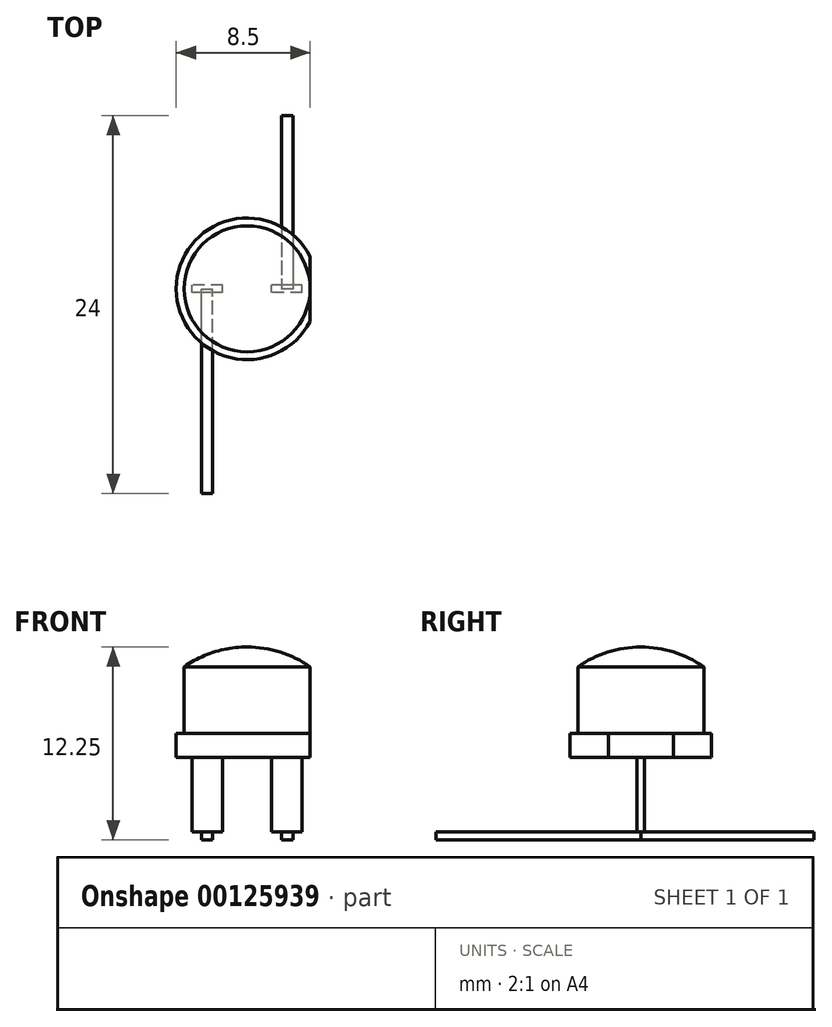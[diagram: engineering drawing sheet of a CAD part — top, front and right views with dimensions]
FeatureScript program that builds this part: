
annotation { "Feature Type Name" : "Feature", "Feature Type Description" : "" }
export const myFeature = defineFeature(function(context is Context, id is Id, definition is map)
    precondition{}
    {
        {
            var Q0;
            Q0=qCreatedBy(makeId("Front.planeOp"),FACE);
            var sketch = newSketch(context, id + "F0", { "sketchPlane" : qUnion([Q0])});
            skLineSegment(sketch, "E0", {"start": v(0, 0) * mm, "end": v(-4.5, 0) * mm});
            skLineSegment(sketch, "E1", {"start": v(-4.5, 0) * mm, "end": v(-4.5, 1.5) * mm});
            skLineSegment(sketch, "E2", {"start": v(-4.5, 1.5) * mm, "end": v(-4, 1.5) * mm});
            skLineSegment(sketch, "E3", {"start": v(-4, 1.5) * mm, "end": v(-4, 5.74) * mm});
            skLineSegment(sketch, "E4", {"start": v(0, 0) * mm, "end": v(0, 7) * mm});
            skArc(sketch, "E5", {"start": v(0, 7) * mm, "mid": v(-2.1, 6.68) * mm, "end": v(-4, 5.74) * mm});
            skSolve(sketch);
        }
        {
            var Q0;
            Q0=qSketchRegion(id+"F0",true);
            var Q1;
            Q1=sQuery(id+"F0.wireOp",EDGE,"E4");
            revolve(context, id + "F1", {"entities" : qUnion([Q0]), "axis" : qUnion([Q1]), "revolveType" : RevolveType.FULL});
        }
        {
            var Q0;
            Q0=makeQuery(id+"F1.opRevolve","SWEPT_FACE",FACE,{"disambiguationData":[OSD([sQuery(id+"F0.wireOp",EDGE,"E0")])]});
            var sketch = newSketch(context, id + "F2", { "sketchPlane" : qUnion([Q0])});
            skLineSegment(sketch, "E6", {"start": v(4, 2.06) * mm, "end": v(4, -2.06) * mm});
            skArc(sketch, "E7", {"start": v(4, -2.06) * mm, "mid": v(4.5, 0) * mm, "end": v(4, 2.06) * mm});
            skSolve(sketch);
        }
        {
            var Q0;
            Q0=qSketchRegion(id+"F2",true);
            extrude(context, id + "F3", {"entities" : qUnion([Q0]), "operationType" : NewBodyOperationType.REMOVE, "endBound" : BoundingType.THROUGH_ALL, "oppositeDirection" : true, "depth" : 25 * mm});
        }
        {
            var Q0;
            Q0=makeQuery(id+"F1.opRevolve","SWEPT_FACE",FACE,{"disambiguationData":[OSD([sQuery(id+"F0.wireOp",EDGE,"E0")])]});
            var sketch = newSketch(context, id + "F4", { "sketchPlane" : qUnion([Q0])});
            skLineSegment(sketch, "E8.bottom", {"start": v(3.5, 0.25) * mm, "end": v(1.55, 0.25) * mm});
            skLineSegment(sketch, "E8.top", {"start": v(3.5, -0.25) * mm, "end": v(1.55, -0.25) * mm});
            skLineSegment(sketch, "E8.left", {"start": v(3.5, 0.25) * mm, "end": v(3.5, -0.25) * mm});
            skLineSegment(sketch, "E8.right", {"start": v(1.55, 0.25) * mm, "end": v(1.55, -0.25) * mm});
            skLineSegment(sketch, "E9.left", {"start": v(-1.55, 0.25) * mm, "end": v(-1.55, -0.25) * mm});
            skLineSegment(sketch, "E9.right", {"start": v(-3.5, 0.25) * mm, "end": v(-3.5, -0.25) * mm});
            skLineSegment(sketch, "E10", {"start": v(-1.55, 0.25) * mm, "end": v(-3.5, 0.25) * mm});
            skLineSegment(sketch, "E11", {"start": v(-1.55, -0.25) * mm, "end": v(-3.5, -0.25) * mm});
            skSolve(sketch);
        }
        {
            var Q0;
            Q0=qSketchRegion(id+"F4",true);
            extrude(context, id + "F5", {"entities" : qUnion([Q0]), "operationType" : NewBodyOperationType.ADD, "depth" : 4.75 * mm});
        }
        {
            var Q0;
            Q0=makeQuery(id+"F5.opExtrude","CAP_FACE",FACE,{"disambiguationData":[OSD([sQuery(id+"F4.wireOp",EDGE,"E8.bottom"),sQuery(id+"F4.wireOp",EDGE,"E8.top"),sQuery(id+"F4.wireOp",EDGE,"E8.left"),sQuery(id+"F4.wireOp",EDGE,"E8.right")])],"isStart":false});
            var sketch = newSketch(context, id + "F6", { "sketchPlane" : qUnion([Q0])});
            skLineSegment(sketch, "E12.bottom", {"start": v(2.9, 0.25) * mm, "end": v(2.2, 0.25) * mm});
            skLineSegment(sketch, "E12.top", {"start": v(2.9, -0.25) * mm, "end": v(2.2, -0.25) * mm});
            skLineSegment(sketch, "E12.left", {"start": v(2.9, 0.25) * mm, "end": v(2.9, -0.25) * mm});
            skLineSegment(sketch, "E12.right", {"start": v(2.2, 0.25) * mm, "end": v(2.2, -0.25) * mm});
            skSolve(sketch);
        }
        {
            var Q0;
            Q0=makeQuery(id+"F5.opExtrude","CAP_FACE",FACE,{"disambiguationData":[OSD([sQuery(id+"F4.wireOp",EDGE,"E9.left"),sQuery(id+"F4.wireOp",EDGE,"E9.right"),sQuery(id+"F4.wireOp",EDGE,"E10"),sQuery(id+"F4.wireOp",EDGE,"E11")])],"isStart":false});
            var sketch = newSketch(context, id + "F7", { "sketchPlane" : qUnion([Q0])});
            skLineSegment(sketch, "E13.bottom", {"start": v(-2.2, 0.25) * mm, "end": v(-2.9, 0.25) * mm});
            skLineSegment(sketch, "E13.top", {"start": v(-2.2, -0.25) * mm, "end": v(-2.9, -0.25) * mm});
            skLineSegment(sketch, "E13.left", {"start": v(-2.2, 0.25) * mm, "end": v(-2.2, -0.25) * mm});
            skLineSegment(sketch, "E13.right", {"start": v(-2.9, 0.25) * mm, "end": v(-2.9, -0.25) * mm});
            skSolve(sketch);
        }
        {
            var Q0;
            Q0=qCreatedBy(makeId("Front.planeOp"),FACE);
            var sketch = newSketch(context, id + "F8", { "sketchPlane" : qUnion([Q0])});
            skLineSegment(sketch, "E14.bottom", {"start": v(-2.9, -4.75) * mm, "end": v(-2.2, -4.75) * mm});
            skLineSegment(sketch, "E14.top", {"start": v(-2.9, -5.25) * mm, "end": v(-2.2, -5.25) * mm});
            skLineSegment(sketch, "E14.left", {"start": v(-2.9, -4.75) * mm, "end": v(-2.9, -5.25) * mm});
            skLineSegment(sketch, "E14.right", {"start": v(-2.2, -4.75) * mm, "end": v(-2.2, -5.25) * mm});
            skSolve(sketch);
        }
        {
            var Q0;
            Q0 = qSketchRegion(id + "F8", true);
            extrude(context, id + "F9", {"entities" : qUnion([Q0]), "operationType" : NewBodyOperationType.ADD, "depth" : 13 * mm});
        }
        {
            var Q0;
            Q0=qCreatedBy(makeId("Front.planeOp"),FACE);
            var sketch = newSketch(context, id + "F10", { "sketchPlane" : qUnion([Q0])});
            skLineSegment(sketch, "E15.bottom", {"start": v(2.9, -4.75) * mm, "end": v(2.2, -4.75) * mm});
            skLineSegment(sketch, "E15.top", {"start": v(2.9, -5.25) * mm, "end": v(2.2, -5.25) * mm});
            skLineSegment(sketch, "E15.left", {"start": v(2.9, -4.75) * mm, "end": v(2.9, -5.25) * mm});
            skLineSegment(sketch, "E15.right", {"start": v(2.2, -4.75) * mm, "end": v(2.2, -5.25) * mm});
            skSolve(sketch);
        }
        {
            var Q0;
            Q0 = qSketchRegion(id + "F10", true);
            extrude(context, id + "F11", {"entities" : qUnion([Q0]), "operationType" : NewBodyOperationType.ADD, "oppositeDirection" : true, "depth" : 11 * mm});
        }
    });
